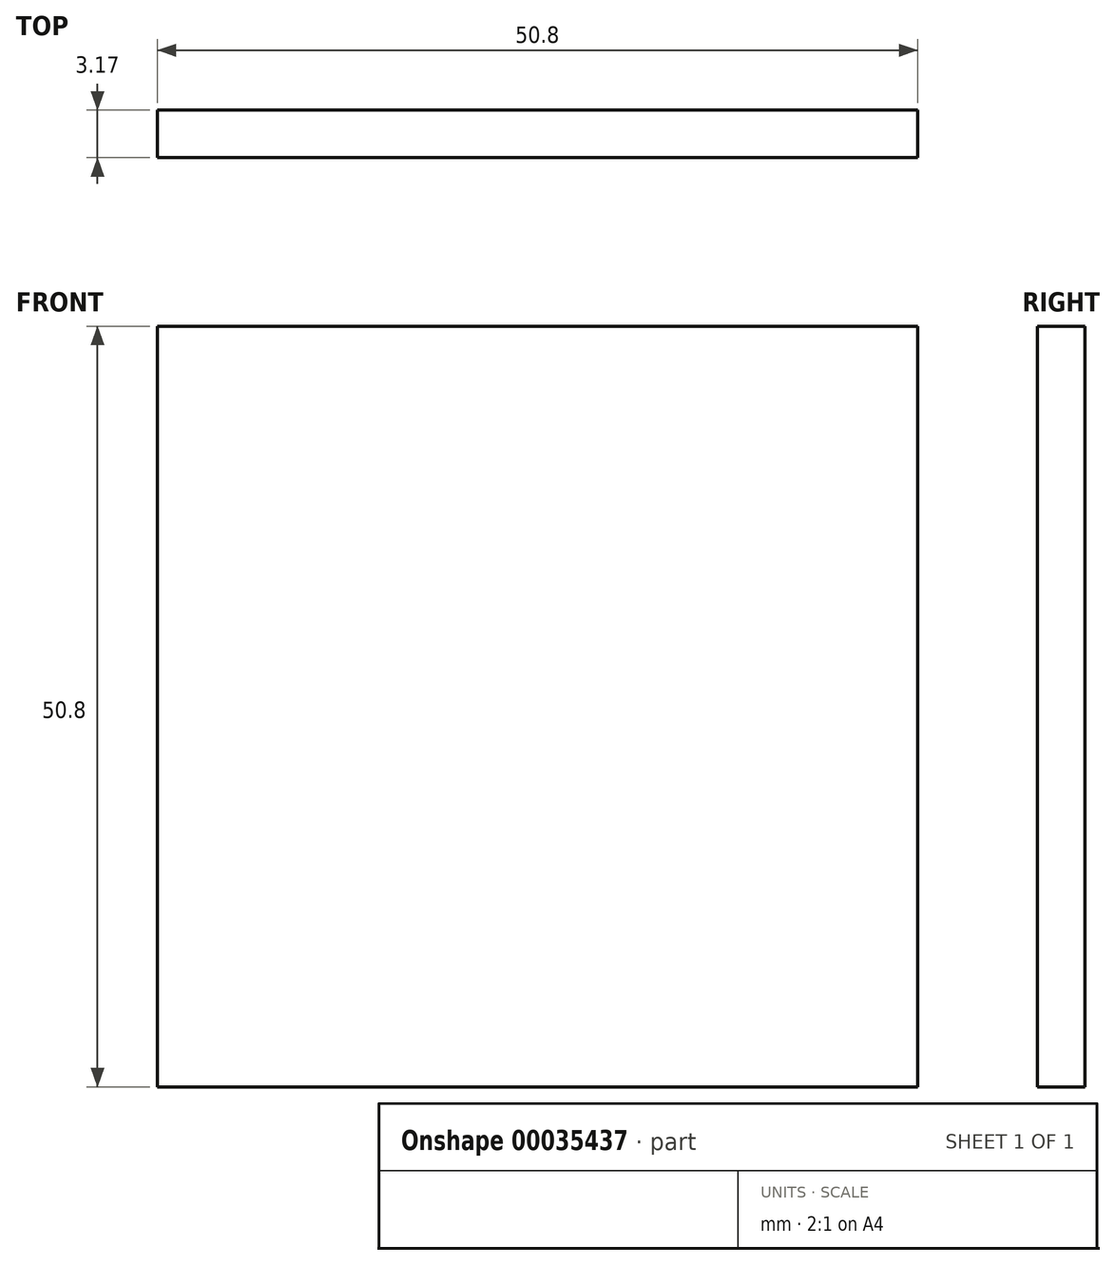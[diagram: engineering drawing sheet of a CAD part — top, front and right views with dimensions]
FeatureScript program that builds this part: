
annotation { "Feature Type Name" : "Feature", "Feature Type Description" : "" }
export const myFeature = defineFeature(function(context is Context, id is Id, definition is map)
    precondition{}
    {
        {
            var Q0;
            Q0=qCreatedBy(makeId("Front.planeOp"),FACE);
            var sketch = newSketch(context, id + "F0", { "sketchPlane" : qUnion([Q0])});
            skLineSegment(sketch, "E0.rect.bottom", {"start": v(25.4, -25.4) * mm, "end": v(-25.4, -25.4) * mm});
            skLineSegment(sketch, "E0.rect.top", {"start": v(25.4, 25.4) * mm, "end": v(-25.4, 25.4) * mm});
            skLineSegment(sketch, "E0.rect.left", {"start": v(25.4, -25.4) * mm, "end": v(25.4, 25.4) * mm});
            skLineSegment(sketch, "E0.rect.right", {"start": v(-25.4, -25.4) * mm, "end": v(-25.4, 25.4) * mm});
            skPoint(sketch, "E0.rect.middle", {"position": v(0, 0) * mm});
            skSolve(sketch);
        }
        {
            var Q0;
            Q0=makeQuery(id+"F0.imprint","IMPRINT",FACE,{"disambiguationData":[TD([[makeQuery(id+"F0.imprint","IMPRINT",EDGE,{"derivedFrom":sQuery(id+"F0.wireOp",EDGE,"E0.rect.bottom")}),-1.0]])]});
            extrude(context, id + "F1", {"entities" : qUnion([Q0]), "depth" : 3.17 * mm});
        }
    });
